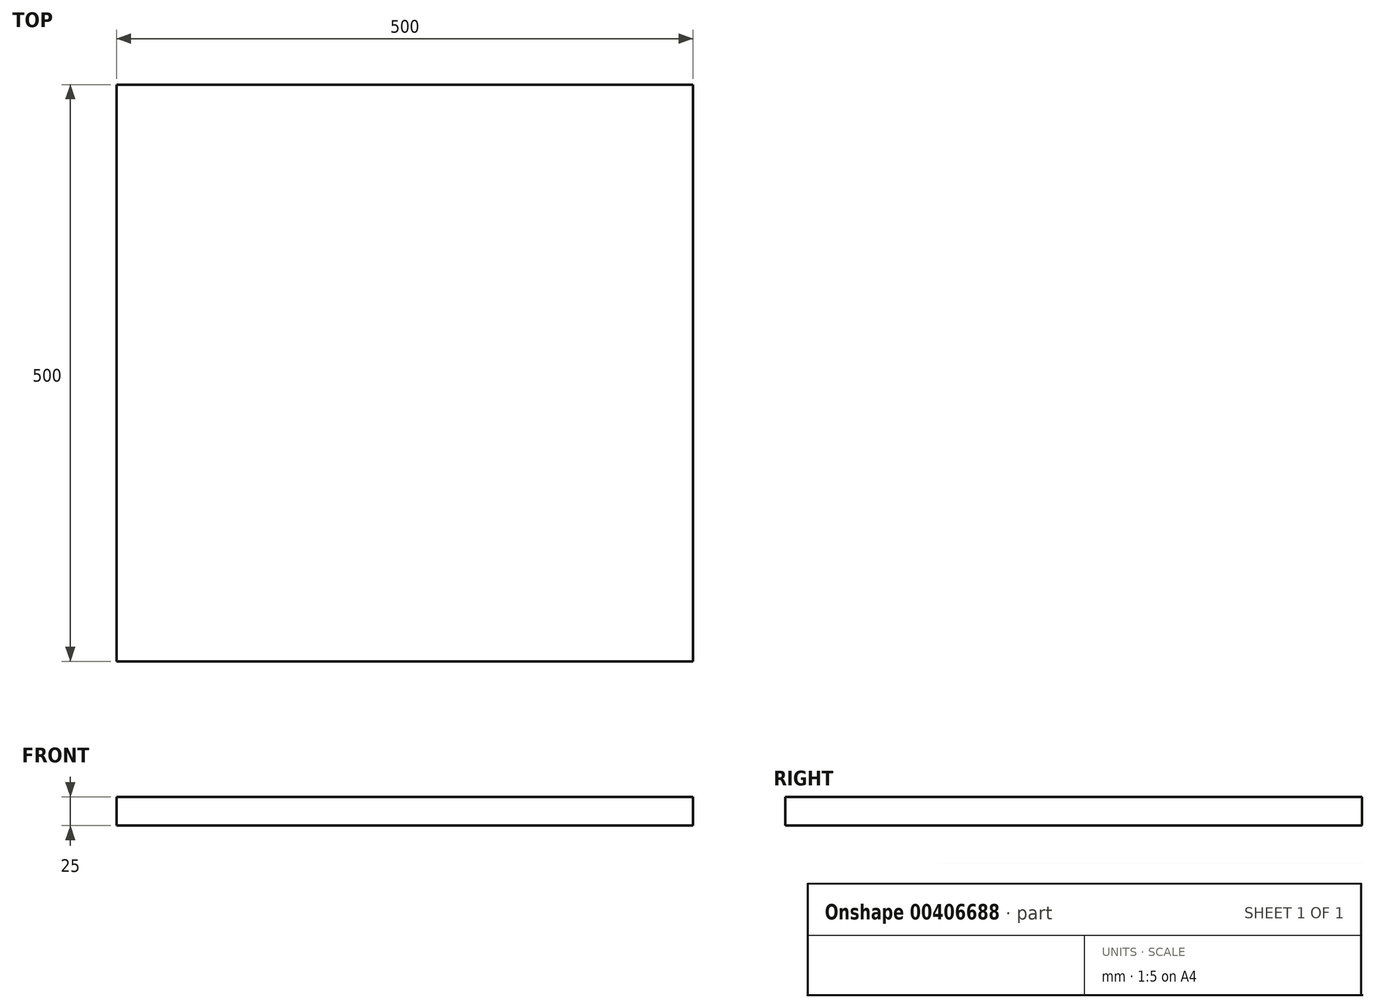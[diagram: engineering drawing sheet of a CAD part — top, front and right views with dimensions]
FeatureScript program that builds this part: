
annotation { "Feature Type Name" : "Feature", "Feature Type Description" : "" }
export const myFeature = defineFeature(function(context is Context, id is Id, definition is map)
    precondition{}
    {
        {
            var Q0;
            Q0=qCreatedBy(makeId("Top.planeOp"),FACE);
            var sketch = newSketch(context, id + "F0", { "sketchPlane" : qUnion([Q0])});
            skLineSegment(sketch, "E0", {"start": v(0, 0) * mm, "end": v(500, 0) * mm});
            skLineSegment(sketch, "E1", {"start": v(500, 0) * mm, "end": v(500, 500) * mm});
            skLineSegment(sketch, "E2", {"start": v(500, 500) * mm, "end": v(0, 500) * mm});
            skLineSegment(sketch, "E3", {"start": v(0, 500) * mm, "end": v(0, 0) * mm});
            skSolve(sketch);
        }
        {
            var Q0;
            Q0 = qSketchRegion(id + "F0", true);
            extrude(context, id + "F1", {"entities" : qUnion([Q0]), "depth" : 25 * mm});
        }
    });
